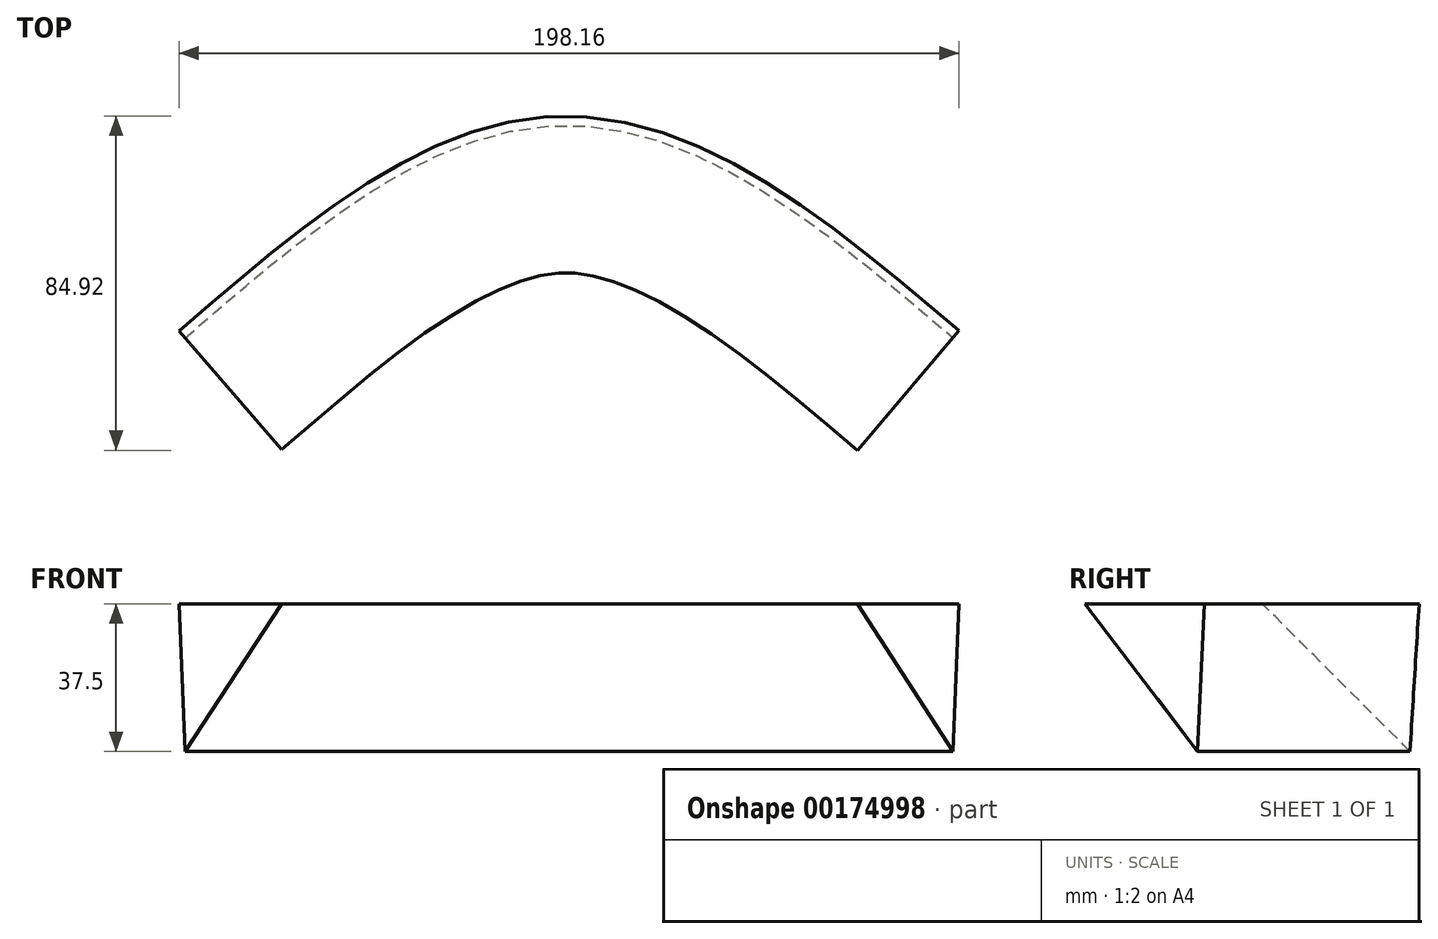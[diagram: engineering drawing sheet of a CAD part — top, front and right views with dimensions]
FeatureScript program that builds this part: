
annotation { "Feature Type Name" : "Feature", "Feature Type Description" : "" }
export const myFeature = defineFeature(function(context is Context, id is Id, definition is map)
    precondition{}
    {
        {
            var Q0;
            Q0=qCreatedBy(makeId("Top.planeOp"),FACE);
            var sketch = newSketch(context, id + "F0", { "sketchPlane" : qUnion([Q0])});
            skLineSegment(sketch, "E0", {"start": v(0, 0) * mm, "end": v(177.8, 0) * mm});
            skPoint(sketch, "E1", {"position": v(88.9, 0) * mm});
            skFitSpline(sketch, "E2", {"points": [v(0, 0) * mm, v(87.9, 50.8) * mm, v(177.8, 0) * mm], "startDerivative": vector(175.91, 152.62) * mm, "endDerivative": vector(179.68, -152.19) * mm});
            skLineSegment(sketch, "E3", {"start": v(0, 0) * mm, "end": v(49.34, 42.81) * mm});
            skLineSegment(sketch, "E4", {"start": v(0, 0) * mm, "end": v(33.4, -38.5) * mm});
            skSolve(sketch);
        }
        {
            var Q0;
            {var subQ0=sQuery(id+"F0.wireOp",EDGE,"j4uQPeyW-IKGc-KB3Q-n13p-uj2LacgPaRta");Q0=makeQuery(id+"F0.imprint","IMPRINT",FACE,{"disambiguationData":[TD([[makeQuery(id+"F0.imprint","IMPRINT",EDGE,{"derivedFrom":subQ0}),1.0]])]});}
            var Q1;
            Q1=sQuery(id+"F0.wireOp",EDGE,"E4");
            var Q2;
            Q2=sQuery(id+"F0.wireOp",EDGE,"E3");
            revolve(context, id + "F1", {"bodyType" : ToolBodyType.SURFACE, "operationType" : NewBodyOperationType.ADD, "entities" : qUnion([Q0]), "surfaceEntities" : qUnion([Q1]), "axis" : qUnion([Q2]), "revolveType" : RevolveType.FULL});
        }
        {
            var Q0;
            Q0=makeQuery(id+"F1.opRevolve","SWEPT_FACE",FACE,{"disambiguationData":[OSD([sQuery(id+"F0.wireOp",EDGE,"E4")])]});
            var sketch = newSketch(context, id + "F2", { "sketchPlane" : qUnion([Q0])});
            skLineSegment(sketch, "E5", {"start": v(13.3, -31.17) * mm, "end": v(-24.21, 6.33) * mm});
            skLineSegment(sketch, "E6", {"start": v(-24.21, 6.33) * mm, "end": v(15.64, 6.33) * mm});
            skLineSegment(sketch, "E7", {"start": v(15.64, 6.33) * mm, "end": v(13.3, -31.17) * mm});
            skSolve(sketch);
        }
        {
            var Q0;
            Q0=makeQuery(id+"F2.imprint","IMPRINT",FACE,{"disambiguationData":[TD([[makeQuery(id+"F2.imprint","IMPRINT",EDGE,{"derivedFrom":sQuery(id+"F2.wireOp",EDGE,"E5")}),-1.0]])]});
            var Q1;
            Q1=sQuery(id+"F0.wireOp",EDGE,"E2");
            sweep(context, id + "F3", {"profiles" : qUnion([Q0]), "path" : qUnion([Q1])});
        }
    });
